# Revit family: 111111003403001
name_source: partatom
category: Modelos genéricos
revit_build: Autodesk Revit 2018 (Build: 20190510_1515(x64)
units: mm (PartAtom-declared; Revit-internal decimal feet)

## family parameters
Anfitrión = Cara
Compartido = No
Corte con vacíos al cargar = No
Cota de conector redondo = Diámetro de uso
Puede alojar armadura = No
Punto de cálculo de habitación = No
Tipo de pieza = Normal

## types (1)
- CELOSIA BEAGLE PAI 35X12.5CM BLANCO
    Color = Blanco
    Dimension = 125 mm  [stored 0.410105 ft]
    Elevación por defecto = 1000 mm  [stored 3.28084 ft]
    Empresa = CNP SPA.
    Espesor = 1 mm  [stored 0.00328084 ft]
    Largo = 350 mm  [stored 1.14829 ft]
    Material = PP Blanco
    Model = CELOSIA BEAGLE PAI
    Nombre SKU = CELOSIA BEAGLE PAI 35X12.5CM BLANCO
    Num SKUs = 111111003403001
    URL = https://www.empresascnp.cl
    Unidad = Cajas de 50 Unidades
    Url Ficha tecnica = https://empresascnp.cl
    Uso = Se utiliza como sistema de ventilación en Puertas, Shaft, Muro y Tina

note: [stored X ft] marks values corroborated as IEEE doubles in the binary element streams (Revit-internal decimal feet)

## geometry (parser evidence)
native form markers: Sweep x10
no freeform markers — native parametric forms only
